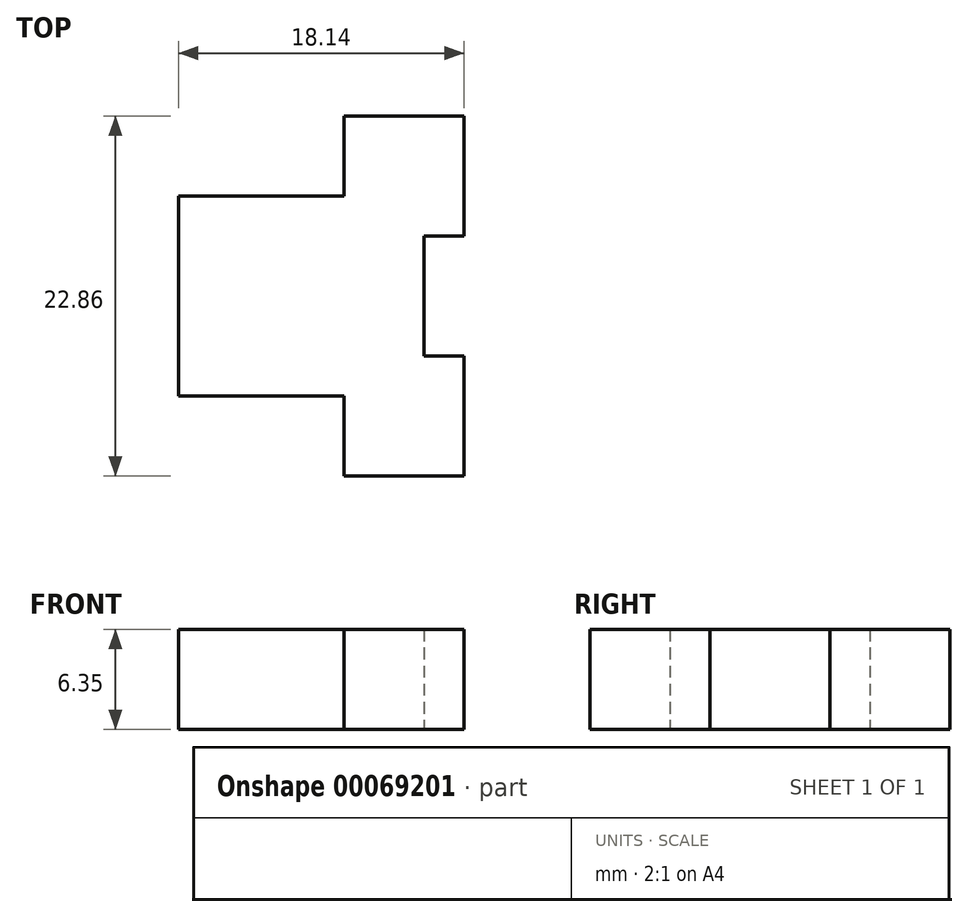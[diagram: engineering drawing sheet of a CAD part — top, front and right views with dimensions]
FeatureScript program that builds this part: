
annotation { "Feature Type Name" : "Feature", "Feature Type Description" : "" }
export const myFeature = defineFeature(function(context is Context, id is Id, definition is map)
    precondition{}
    {
        {
            var Q0;
            Q0=qCreatedBy(makeId("Top.planeOp"),FACE);
            var sketch = newSketch(context, id + "F0", { "sketchPlane" : qUnion([Q0])});
            skLineSegment(sketch, "E0.rect.bottom", {"start": v(-1.29, 0) * mm, "end": v(-11.8, 0) * mm});
            skLineSegment(sketch, "E0.rect.top", {"start": v(-1.29, 12.7) * mm, "end": v(-11.8, 12.7) * mm});
            skLineSegment(sketch, "E0.rect.left", {"start": v(-1.29, 0) * mm, "end": v(-1.29, 12.7) * mm});
            skLineSegment(sketch, "E0.rect.right", {"start": v(-11.8, 0) * mm, "end": v(-11.8, 12.7) * mm});
            skPoint(sketch, "E0.rect.middle", {"position": v(-6.55, 6.35) * mm});
            skLineSegment(sketch, "E1", {"start": v(-1.29, 12.7) * mm, "end": v(-1.29, 17.78) * mm});
            skLineSegment(sketch, "E2", {"start": v(-1.29, 17.78) * mm, "end": v(6.33, 17.78) * mm});
            skLineSegment(sketch, "E3", {"start": v(6.33, 17.78) * mm, "end": v(6.33, 10.16) * mm});
            skLineSegment(sketch, "E4", {"start": v(6.33, 10.16) * mm, "end": v(3.8, 10.16) * mm});
            skLineSegment(sketch, "E5", {"start": v(3.8, 10.16) * mm, "end": v(3.8, 2.54) * mm});
            skLineSegment(sketch, "E6", {"start": v(3.8, 2.54) * mm, "end": v(6.33, 2.54) * mm});
            skLineSegment(sketch, "E7", {"start": v(6.33, 2.54) * mm, "end": v(6.33, -5.08) * mm});
            skLineSegment(sketch, "E8", {"start": v(6.33, -5.08) * mm, "end": v(-1.29, -5.08) * mm});
            skLineSegment(sketch, "E9", {"start": v(-1.29, -5.08) * mm, "end": v(-1.29, 0) * mm});
            skSolve(sketch);
        }
        {
            var Q0;
            Q0 = qSketchRegion(id + "F0", true);
            extrude(context, id + "F1", {"entities" : qUnion([Q0]), "depth" : 6.35 * mm});
        }
    });
